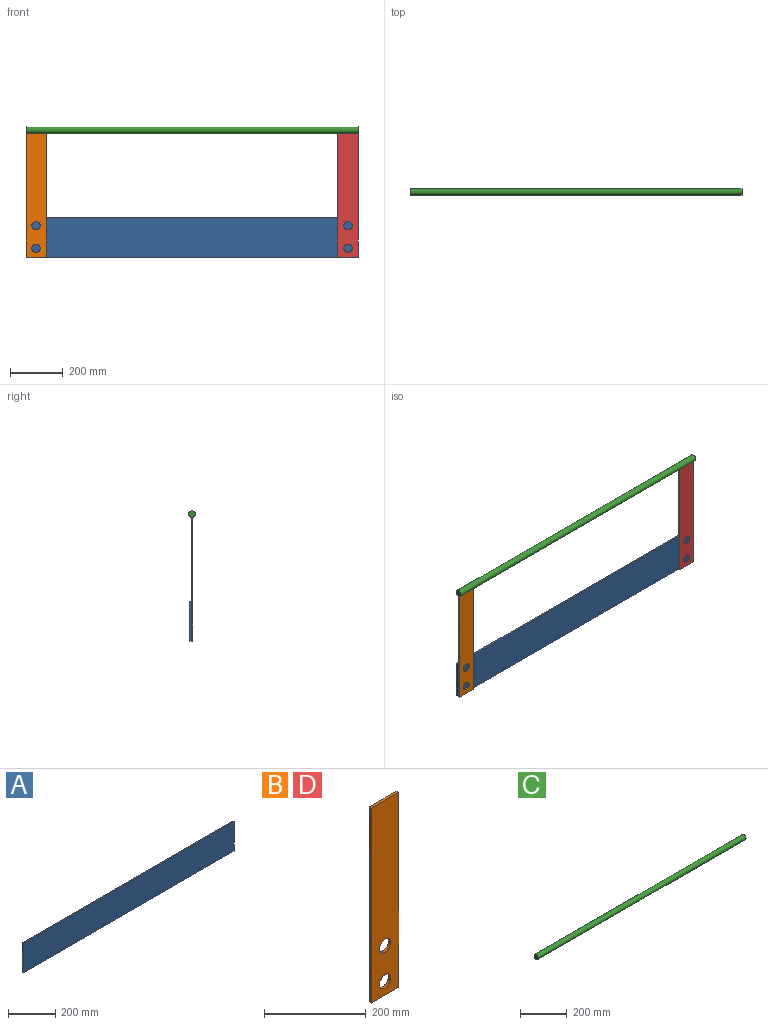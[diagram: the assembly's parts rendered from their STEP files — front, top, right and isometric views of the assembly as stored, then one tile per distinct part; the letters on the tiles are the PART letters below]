
ASSEMBLY  parts=4 mates=2
PART A: 6 faces, bbox 1263.7x6.4x152.4 mm
  f0: plane 1263.65x6.35mm, normal (0,0,1), area 8024.2mm2, adj f1,f3,f4,f5
  f1: plane 152.4x6.35mm, normal (-1,0,0), area 967.7mm2, adj f0,f2,f4,f5
  f2: plane 1263.65x6.35mm, normal (0,0,-1), area 8024.2mm2, adj f1,f3,f4,f5
  f3: plane 152.4x6.35mm, normal (1,0,0), area 967.7mm2, adj f0,f2,f4,f5
  f4: plane 1263.65x152.4mm, normal (0,-1,0), area 192580.3mm2, adj f0,f1,f2,f3
  f5: plane 1263.65x152.4mm, normal (0,1,0), area 192580.3mm2, adj f0,f1,f2,f3
PART B: 8 faces, bbox 76.2x6.4x469.9 mm
  f0: plane 76.2x6.35mm, normal (0,0,-1), area 483.9mm2, adj f1,f5,f6,f7
  f1: plane 469.9x6.35mm, normal (1,0,0), area 2983.9mm2, adj f0,f2,f6,f7
  f2: plane 76.2x6.35mm, normal (0,0,1), area 483.9mm2, adj f1,f5,f6,f7
  f3: cylinder r=15.88mm len=31.75mm, axis (0,1,0), area 633.4mm2, adj f6,f7
  f4: cylinder r=15.88mm len=31.75mm, axis (0,1,0), area 633.4mm2, adj f6,f7
  f5: plane 469.9x6.35mm, normal (-1,0,0), area 2983.9mm2, adj f0,f2,f6,f7
  f6: plane 469.9x76.2mm, normal (0,-1,0), area 34222.9mm2, adj f0,f1,f2,f3,f4,f5
  f7: plane 469.9x76.2mm, normal (0,1,0), area 34222.9mm2, adj f0,f1,f2,f3,f4,f5
PART C: 3 faces, bbox 1263.7x25.4x25.4 mm
  f0: cylinder r=12.7mm len=1263.65mm, axis (-1,0,0), area 100834.8mm2, adj f1,f2
  f1: plane 25.4x25.4mm, normal (1,0,0), area 506.7mm2, adj f0
  f2: plane 25.4x25.4mm, normal (-1,0,0), area 506.7mm2, adj f0
PART D: same geometry as B
PLACE A t=(-506.51,227.86,-103.49)mm
PLACE B t=(-123.9,215.16,-77.27)mm
PLACE C t=(469.82,211.99,-99.53)mm
PLACE D t=(1063.55,215.16,-77.27)mm
MATE fastened A.f4 <-> D.f7  axis (0,-1,0) through (1101.65,215.16,-312.22)mm
MATE fastened C.f0 <-> B.f5  axis (-1,0,0) through (-162,211.99,170.38)mm
